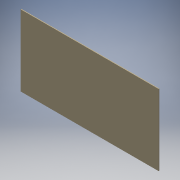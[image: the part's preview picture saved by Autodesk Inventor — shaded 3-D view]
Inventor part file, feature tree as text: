
AUTODESK INVENTOR PART (.ipt)
format: ipt  version: 2019 (Build 230136000, 136)  size: 89,088 bytes
history: native  units: mm
features: extrude x1, sketch x1
ambient origin geometry x8: Origin, YZ Plane, XZ Plane, XY Plane, X Axis, Y Axis, Z Axis, Center Point
bodies: Solid1 (feature_tree)
feature tree (2):
  extrude  "Extrusion1"  Depth=861.06mm
  sketch  "Sketch1"  dims[d0=4.7625mm d1=0.0mm d2=861.06mm d3=444.5mm]
